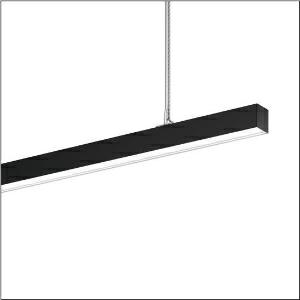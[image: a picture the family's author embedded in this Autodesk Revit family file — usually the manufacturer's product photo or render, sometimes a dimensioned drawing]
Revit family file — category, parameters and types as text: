
# Revit family: silica_r__21_51mx33db49bb_8fe2
name_source: partatom
category: Lighting Fixtures
units: mm (PartAtom-declared; Revit-internal decimal feet)

## family parameters
Cut with Voids When Loaded = No
Host = Face
Light Source = No
Part Type = Normal
Room Calculation Point = No
Round Connector Dimension = Use Diameter
Shared = No

## types (1)
- --- (1 x LED, 7390 lm, 48.3 W, 4000K)
    Apparent Load = 48 VA
    CIE Flux Codes = 78 96 99 55 100
    Color Rendering = 80
    Color Temperature = 4000K
    Default Elevation = 1800 mm
    Description = Silica® 21, office luminaire, primary optical cover: prismatic diffuser, of PMMA, CAT 2 (L<= 3000cd/m²), light emission: direct/indirect distribution, primary light characteristic: symmetric, installation type: suspended mounting, LED, rated luminous flux: 7.390lm, luminous efficacy: 153lm/W, light colour: 840, colour temperature: 4000K, with terminal, 3+2-pole, max. 2.5mm², mains connection: 220..240V, AC, 50/60Hz, rated input power: 48.3W, luminaire housing, of aluminium, jet black (RAL 9005), length: 1.504mm, width: 53mm, height: 53mm, protection rating (complete): IP20, insulation class (complete): insulation class I (protective earthing), certification: CE, permissible operating ambient temperature: 0..+35°C, standard: EN 50419, packaging unit: 1 piece
    Height = 53 mm
    Lamp = 1 x LED
    Lamp Light Flux = 7390 lm
    Lamp Power = 48.3 W
    Lamp count = 1
    Length = 1504 mm
    Luminous efficacy = 153 lm/W
    Manufacturer = Siteco
    ModVariant = No
    Model = 51MX33DB49BB
    Mounting Place = Ceiling
    Mounting Type = Pendant
    Number of Poles = 1
    OnlyDefault = Yes
    Power Factor = 1
    Product Name = Silica® 21
    Product group = office luminaire | ceiling pendant
    ProductGroupID = 902
    Protection Class = Protection class I
    Protection Degree = IP 20
    RLX_Detail_Level = 1
    RLX_Emergency_Light_Flux = 0 lm
    RLX_Emergency_Type = 0
    RLX_Emergency_Type_DB = No
    RlxData = <blob elided: 26145 chars, md5=ceda85f7>
    Socket = socket
    Standby Power = 0 W
    System Light Flux = 7390 lm
    System Power = 48 W
    Type Comments = factory setting: luminous flux: 100 % | dim-lin: 254 | 323 mA
    Type Image = l_1313646.jpg
    URL = http://relux.com
    VarID = @adj_066937
    Voltage = 0 V
    Weight = 0.00 kg
    Width = 53 mm

## geometry (parser evidence)
native form markers: Blend x4, Sweep x13
no freeform markers — native parametric forms only
